# Revit family: QF_MACOM_HOSIM65A-2M
name_source: partatom
category: Equipamento especial
units: mm (PartAtom-declared; Revit-internal decimal feet)

## family parameters
Com base no plano de trabalho = Não
Compartilhado = Não
Corte com vazios quando carregada = Não
Cota do conector redondo = Utilizar diâmetro
Número OmniClass = 23.40.40.14.27
Ponto de cálculo do ambiente = Não
Sempre na vertical = Sim
Tipo de parte = Normal
Título OmniClass = Ice Machines

## types (1)
- HOSIM65A-2M
    Apparent Power = 0 VA
    Cold Water Connection Height = 229 mm
    Cold Water Flow = 0,0 L/s
    Cold Water Maximum Pressure = 0,0 Pa
    Cold Water Minimum Pressure = 0,0 Pa
    Cold Water RI Height = 0 mm
    Cold Water Size = 1/2"
    Cold Water Temperature Recommended = 0 °C
    Conn Conduit = Sim
    Descrição = MAQUINA DE GELO EM CUBO HOSHIZAKI, PRODUCAO ATE 62KG/DIA, COM DEPOSITO DE 26KG - 220V MONOF - IM-65A-660X570X932mm
    Elec Conn RI Height = 0 mm
    Elevação padrão = 0 mm
    FL Amps = 0 A
    Fabricante = MACOM
    Height Actual = 932 mm
    Indirect Waste Connection Height = 153 mm
    Indirect Waste Flow = 0,0 L/s
    Indirect Waste Size = 1"
    Max Overcurrent Protection = 0 A
    Min Ckt Ampacity = 0 A
    Modelo = HOSIM65A-2M
    Number of Poles = 0
    Production per Cycle = 42 cubes
    Production per Day = 0
    Storage = 26,00 kg
    URL = https://www.acosmacom.com.br
    Volume = 0,33 m³
    Waste Water Discharge Temperature = 0 °C
    Water Consumption per day = 0
    Water Temperature = 0
    Work Temperature = 0

## geometry (parser evidence)
native form markers: Blend x4, Sweep x1
no freeform markers — native parametric forms only
